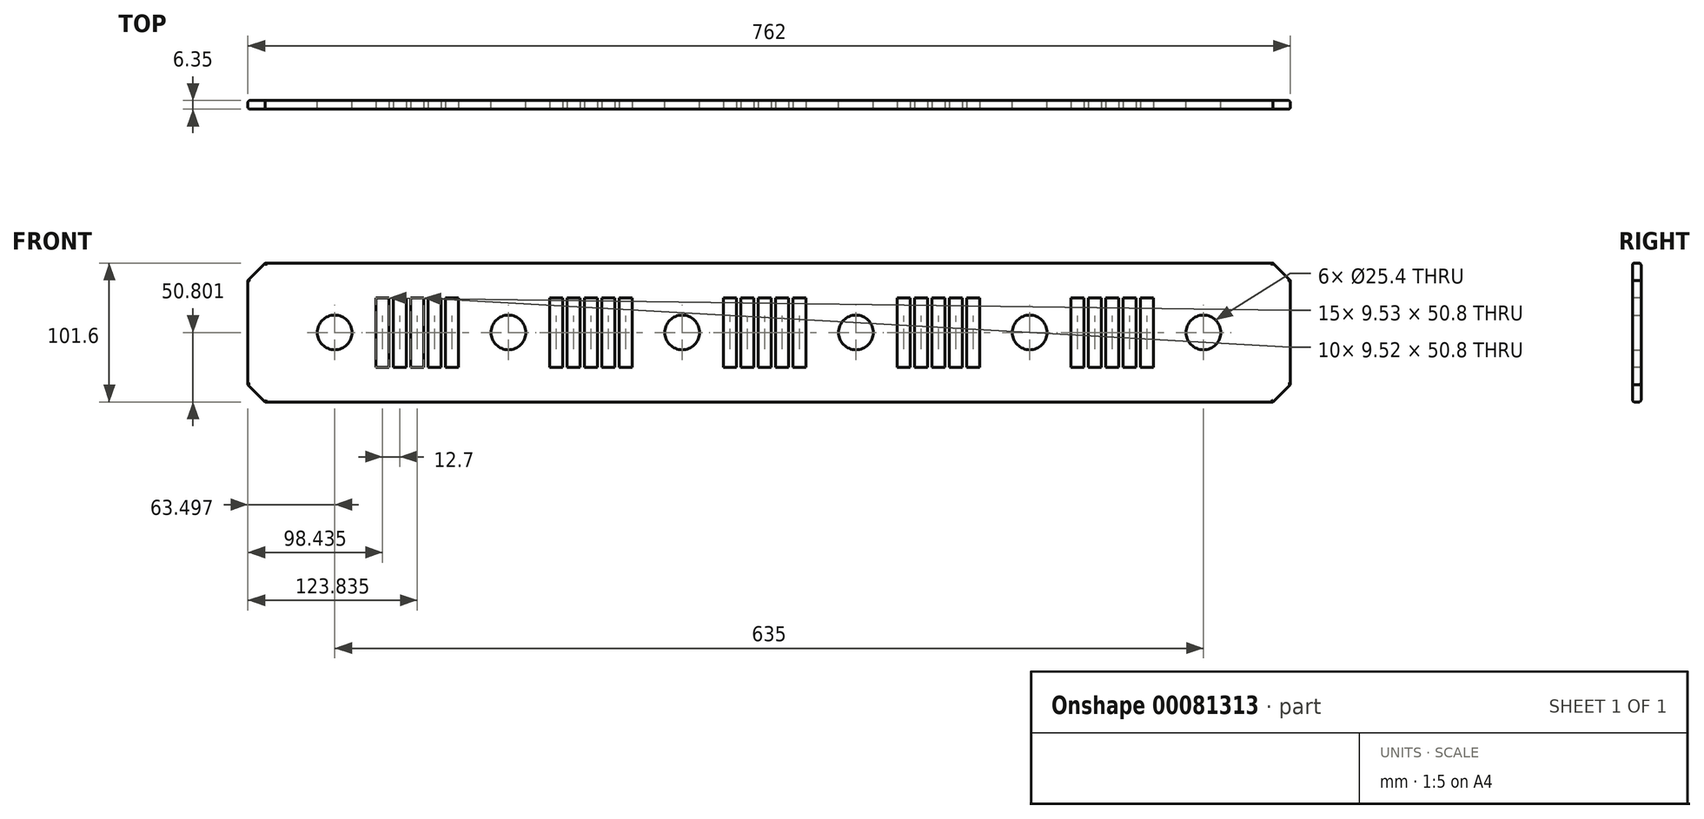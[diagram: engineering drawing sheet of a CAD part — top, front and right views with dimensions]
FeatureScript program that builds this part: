
annotation { "Feature Type Name" : "Feature", "Feature Type Description" : "" }
export const myFeature = defineFeature(function(context is Context, id is Id, definition is map)
    precondition{}
    {
        {
            var Q0;
            Q0=qCreatedBy(makeId("Front.planeOp"),FACE);
            var sketch = newSketch(context, id + "F0", { "sketchPlane" : qUnion([Q0])});
            skLineSegment(sketch, "E0", {"start": v(-386.11, -75.58) * mm, "end": v(375.89, -75.58) * mm});
            skLineSegment(sketch, "E1", {"start": v(375.89, -75.58) * mm, "end": v(375.89, -177.18) * mm});
            skLineSegment(sketch, "E2", {"start": v(375.89, -177.18) * mm, "end": v(-386.11, -177.18) * mm});
            skLineSegment(sketch, "E3", {"start": v(-386.11, -177.18) * mm, "end": v(-386.11, -75.58) * mm});
            skCircle(sketch, "E4", {"center": v(-322.61, -126.38) * mm, "radius": 12.7 * mm});
            skCircle(sketch, "E5", {"center": v(-195.61, -126.38) * mm, "radius": 12.7 * mm});
            skCircle(sketch, "E6", {"center": v(-68.61, -126.38) * mm, "radius": 12.7 * mm});
            skCircle(sketch, "E7", {"center": v(58.39, -126.38) * mm, "radius": 12.7 * mm});
            skCircle(sketch, "E8", {"center": v(185.39, -126.38) * mm, "radius": 12.7 * mm});
            skCircle(sketch, "E9", {"center": v(312.39, -126.38) * mm, "radius": 12.7 * mm});
            skSolve(sketch);
        }
        {
            var Q0;
            Q0 = qSketchRegion(id + "F0", true);
            extrude(context, id + "F1", {"entities" : qUnion([Q0]), "depth" : 6.35 * mm});
        }
        {
            var Q0;
            Q0=makeQuery(id+"F1.opExtrude","CAP_FACE",FACE,{"disambiguationData":[OSD([sQuery(id+"F0.wireOp",EDGE,"E0"),sQuery(id+"F0.wireOp",EDGE,"E1"),sQuery(id+"F0.wireOp",EDGE,"E2"),sQuery(id+"F0.wireOp",EDGE,"E3"),sQuery(id+"F0.wireOp",EDGE,"E4"),sQuery(id+"F0.wireOp",EDGE,"E5"),sQuery(id+"F0.wireOp",EDGE,"E7"),sQuery(id+"F0.wireOp",EDGE,"E6"),sQuery(id+"F0.wireOp",EDGE,"E8"),sQuery(id+"F0.wireOp",EDGE,"E9")])],"isStart":false});
            var sketch = newSketch(context, id + "F2", { "sketchPlane" : qUnion([Q0])});
            skLineSegment(sketch, "E10.bottom", {"start": v(-292.44, -100.98) * mm, "end": v(-282.91, -100.98) * mm});
            skLineSegment(sketch, "E10.top", {"start": v(-292.44, -151.78) * mm, "end": v(-282.91, -151.78) * mm});
            skLineSegment(sketch, "E10.left", {"start": v(-292.44, -100.98) * mm, "end": v(-292.44, -151.78) * mm});
            skLineSegment(sketch, "E10.right", {"start": v(-282.91, -100.98) * mm, "end": v(-282.91, -151.78) * mm});
            skLineSegment(sketch, "E11.1.0.0", {"start": v(-270.21, -100.98) * mm, "end": v(-270.21, -151.78) * mm});
            skLineSegment(sketch, "E11.1.0.1", {"start": v(-279.74, -100.98) * mm, "end": v(-279.74, -151.78) * mm});
            skLineSegment(sketch, "E11.1.0.2", {"start": v(-279.74, -151.78) * mm, "end": v(-270.21, -151.78) * mm});
            skLineSegment(sketch, "E11.1.0.3", {"start": v(-279.74, -100.98) * mm, "end": v(-270.21, -100.98) * mm});
            skLineSegment(sketch, "E11.2.0.0", {"start": v(-257.51, -100.98) * mm, "end": v(-257.51, -151.78) * mm});
            skLineSegment(sketch, "E11.2.0.1", {"start": v(-267.04, -100.98) * mm, "end": v(-267.04, -151.78) * mm});
            skLineSegment(sketch, "E11.2.0.2", {"start": v(-267.04, -151.78) * mm, "end": v(-257.51, -151.78) * mm});
            skLineSegment(sketch, "E11.2.0.3", {"start": v(-267.04, -100.98) * mm, "end": v(-257.51, -100.98) * mm});
            skLineSegment(sketch, "E11.3.0.0", {"start": v(-244.81, -100.98) * mm, "end": v(-244.81, -151.78) * mm});
            skLineSegment(sketch, "E11.3.0.1", {"start": v(-254.34, -100.98) * mm, "end": v(-254.34, -151.78) * mm});
            skLineSegment(sketch, "E11.3.0.2", {"start": v(-254.34, -151.78) * mm, "end": v(-244.81, -151.78) * mm});
            skLineSegment(sketch, "E11.3.0.3", {"start": v(-254.34, -100.98) * mm, "end": v(-244.81, -100.98) * mm});
            skLineSegment(sketch, "E11.4.0.0", {"start": v(-232.11, -100.98) * mm, "end": v(-232.11, -151.78) * mm});
            skLineSegment(sketch, "E11.4.0.1", {"start": v(-241.64, -100.98) * mm, "end": v(-241.64, -151.78) * mm});
            skLineSegment(sketch, "E11.4.0.2", {"start": v(-241.64, -151.78) * mm, "end": v(-232.11, -151.78) * mm});
            skLineSegment(sketch, "E11.4.0.3", {"start": v(-241.64, -100.98) * mm, "end": v(-232.11, -100.98) * mm});
            skLineSegment(sketch, "E11.direction1", {"start": v(-282.91, -151.78) * mm, "end": v(-270.21, -151.78) * mm, "construction": true});
            skLineSegment(sketch, "E12.bottom", {"start": v(-165.44, -100.98) * mm, "end": v(-155.91, -100.98) * mm});
            skLineSegment(sketch, "E12.top", {"start": v(-165.44, -151.78) * mm, "end": v(-155.91, -151.78) * mm});
            skLineSegment(sketch, "E12.left", {"start": v(-165.44, -100.98) * mm, "end": v(-165.44, -151.78) * mm});
            skLineSegment(sketch, "E12.right", {"start": v(-155.91, -100.98) * mm, "end": v(-155.91, -151.78) * mm});
            skLineSegment(sketch, "E13.1.0.0", {"start": v(-143.21, -100.98) * mm, "end": v(-143.21, -151.78) * mm});
            skLineSegment(sketch, "E13.1.0.1", {"start": v(-152.74, -100.98) * mm, "end": v(-152.74, -151.78) * mm});
            skLineSegment(sketch, "E13.1.0.2", {"start": v(-152.74, -151.78) * mm, "end": v(-143.21, -151.78) * mm});
            skLineSegment(sketch, "E13.1.0.3", {"start": v(-152.74, -100.98) * mm, "end": v(-143.21, -100.98) * mm});
            skLineSegment(sketch, "E13.2.0.0", {"start": v(-130.51, -100.98) * mm, "end": v(-130.51, -151.78) * mm});
            skLineSegment(sketch, "E13.2.0.1", {"start": v(-140.04, -100.98) * mm, "end": v(-140.04, -151.78) * mm});
            skLineSegment(sketch, "E13.2.0.2", {"start": v(-140.04, -151.78) * mm, "end": v(-130.51, -151.78) * mm});
            skLineSegment(sketch, "E13.2.0.3", {"start": v(-140.04, -100.98) * mm, "end": v(-130.51, -100.98) * mm});
            skLineSegment(sketch, "E13.3.0.0", {"start": v(-117.81, -100.98) * mm, "end": v(-117.81, -151.78) * mm});
            skLineSegment(sketch, "E13.3.0.1", {"start": v(-127.34, -100.98) * mm, "end": v(-127.34, -151.78) * mm});
            skLineSegment(sketch, "E13.3.0.2", {"start": v(-127.34, -151.78) * mm, "end": v(-117.81, -151.78) * mm});
            skLineSegment(sketch, "E13.3.0.3", {"start": v(-127.34, -100.98) * mm, "end": v(-117.81, -100.98) * mm});
            skLineSegment(sketch, "E13.4.0.0", {"start": v(-105.11, -100.98) * mm, "end": v(-105.11, -151.78) * mm});
            skLineSegment(sketch, "E13.4.0.1", {"start": v(-114.64, -100.98) * mm, "end": v(-114.64, -151.78) * mm});
            skLineSegment(sketch, "E13.4.0.2", {"start": v(-114.64, -151.78) * mm, "end": v(-105.11, -151.78) * mm});
            skLineSegment(sketch, "E13.4.0.3", {"start": v(-114.64, -100.98) * mm, "end": v(-105.11, -100.98) * mm});
            skLineSegment(sketch, "E13.direction1", {"start": v(-155.91, -151.78) * mm, "end": v(-143.21, -151.78) * mm, "construction": true});
            skLineSegment(sketch, "E14.bottom", {"start": v(-38.44, -100.98) * mm, "end": v(-28.91, -100.98) * mm});
            skLineSegment(sketch, "E14.top", {"start": v(-38.44, -151.78) * mm, "end": v(-28.91, -151.78) * mm});
            skLineSegment(sketch, "E14.left", {"start": v(-38.44, -100.98) * mm, "end": v(-38.44, -151.78) * mm});
            skLineSegment(sketch, "E14.right", {"start": v(-28.91, -100.98) * mm, "end": v(-28.91, -151.78) * mm});
            skLineSegment(sketch, "E15.1.0.0", {"start": v(-16.21, -100.98) * mm, "end": v(-16.21, -151.78) * mm});
            skLineSegment(sketch, "E15.1.0.1", {"start": v(-25.74, -100.98) * mm, "end": v(-25.74, -151.78) * mm});
            skLineSegment(sketch, "E15.1.0.2", {"start": v(-25.74, -151.78) * mm, "end": v(-16.21, -151.78) * mm});
            skLineSegment(sketch, "E15.1.0.3", {"start": v(-25.74, -100.98) * mm, "end": v(-16.21, -100.98) * mm});
            skLineSegment(sketch, "E15.2.0.0", {"start": v(-3.51, -100.98) * mm, "end": v(-3.51, -151.78) * mm});
            skLineSegment(sketch, "E15.2.0.1", {"start": v(-13.04, -100.98) * mm, "end": v(-13.04, -151.78) * mm});
            skLineSegment(sketch, "E15.2.0.2", {"start": v(-13.04, -151.78) * mm, "end": v(-3.51, -151.78) * mm});
            skLineSegment(sketch, "E15.2.0.3", {"start": v(-13.04, -100.98) * mm, "end": v(-3.51, -100.98) * mm});
            skLineSegment(sketch, "E15.3.0.0", {"start": v(9.19, -100.98) * mm, "end": v(9.19, -151.78) * mm});
            skLineSegment(sketch, "E15.3.0.1", {"start": v(-0.34, -100.98) * mm, "end": v(-0.34, -151.78) * mm});
            skLineSegment(sketch, "E15.3.0.2", {"start": v(-0.34, -151.78) * mm, "end": v(9.19, -151.78) * mm});
            skLineSegment(sketch, "E15.3.0.3", {"start": v(-0.34, -100.98) * mm, "end": v(9.19, -100.98) * mm});
            skLineSegment(sketch, "E15.4.0.0", {"start": v(21.89, -100.98) * mm, "end": v(21.89, -151.78) * mm});
            skLineSegment(sketch, "E15.4.0.1", {"start": v(12.36, -100.98) * mm, "end": v(12.36, -151.78) * mm});
            skLineSegment(sketch, "E15.4.0.2", {"start": v(12.36, -151.78) * mm, "end": v(21.89, -151.78) * mm});
            skLineSegment(sketch, "E15.4.0.3", {"start": v(12.36, -100.98) * mm, "end": v(21.89, -100.98) * mm});
            skLineSegment(sketch, "E15.direction1", {"start": v(-28.91, -151.78) * mm, "end": v(-16.21, -151.78) * mm, "construction": true});
            skLineSegment(sketch, "E16.bottom", {"start": v(88.56, -100.98) * mm, "end": v(98.09, -100.98) * mm});
            skLineSegment(sketch, "E16.top", {"start": v(88.56, -151.78) * mm, "end": v(98.09, -151.78) * mm});
            skLineSegment(sketch, "E16.left", {"start": v(88.56, -100.98) * mm, "end": v(88.56, -151.78) * mm});
            skLineSegment(sketch, "E16.right", {"start": v(98.09, -100.98) * mm, "end": v(98.09, -151.78) * mm});
            skLineSegment(sketch, "E17.1.0.0", {"start": v(110.79, -100.98) * mm, "end": v(110.79, -151.78) * mm});
            skLineSegment(sketch, "E17.1.0.1", {"start": v(101.26, -100.98) * mm, "end": v(101.26, -151.78) * mm});
            skLineSegment(sketch, "E17.1.0.2", {"start": v(101.26, -151.78) * mm, "end": v(110.79, -151.78) * mm});
            skLineSegment(sketch, "E17.1.0.3", {"start": v(101.26, -100.98) * mm, "end": v(110.79, -100.98) * mm});
            skLineSegment(sketch, "E17.2.0.0", {"start": v(123.49, -100.98) * mm, "end": v(123.49, -151.78) * mm});
            skLineSegment(sketch, "E17.2.0.1", {"start": v(113.96, -100.98) * mm, "end": v(113.96, -151.78) * mm});
            skLineSegment(sketch, "E17.2.0.2", {"start": v(113.96, -151.78) * mm, "end": v(123.49, -151.78) * mm});
            skLineSegment(sketch, "E17.2.0.3", {"start": v(113.96, -100.98) * mm, "end": v(123.49, -100.98) * mm});
            skLineSegment(sketch, "E17.3.0.0", {"start": v(136.19, -100.98) * mm, "end": v(136.19, -151.78) * mm});
            skLineSegment(sketch, "E17.3.0.1", {"start": v(126.66, -100.98) * mm, "end": v(126.66, -151.78) * mm});
            skLineSegment(sketch, "E17.3.0.2", {"start": v(126.66, -151.78) * mm, "end": v(136.19, -151.78) * mm});
            skLineSegment(sketch, "E17.3.0.3", {"start": v(126.66, -100.98) * mm, "end": v(136.19, -100.98) * mm});
            skLineSegment(sketch, "E17.4.0.0", {"start": v(148.89, -100.98) * mm, "end": v(148.89, -151.78) * mm});
            skLineSegment(sketch, "E17.4.0.1", {"start": v(139.36, -100.98) * mm, "end": v(139.36, -151.78) * mm});
            skLineSegment(sketch, "E17.4.0.2", {"start": v(139.36, -151.78) * mm, "end": v(148.89, -151.78) * mm});
            skLineSegment(sketch, "E17.4.0.3", {"start": v(139.36, -100.98) * mm, "end": v(148.89, -100.98) * mm});
            skLineSegment(sketch, "E17.direction1", {"start": v(98.09, -151.78) * mm, "end": v(110.79, -151.78) * mm, "construction": true});
            skLineSegment(sketch, "E18.bottom", {"start": v(215.56, -100.98) * mm, "end": v(225.09, -100.98) * mm});
            skLineSegment(sketch, "E18.top", {"start": v(215.56, -151.78) * mm, "end": v(225.09, -151.78) * mm});
            skLineSegment(sketch, "E18.left", {"start": v(215.56, -100.98) * mm, "end": v(215.56, -151.78) * mm});
            skLineSegment(sketch, "E18.right", {"start": v(225.09, -100.98) * mm, "end": v(225.09, -151.78) * mm});
            skLineSegment(sketch, "E19.1.0.0", {"start": v(237.79, -100.98) * mm, "end": v(237.79, -151.78) * mm});
            skLineSegment(sketch, "E19.1.0.1", {"start": v(228.26, -100.98) * mm, "end": v(228.26, -151.78) * mm});
            skLineSegment(sketch, "E19.1.0.2", {"start": v(228.26, -151.78) * mm, "end": v(237.79, -151.78) * mm});
            skLineSegment(sketch, "E19.1.0.3", {"start": v(228.26, -100.98) * mm, "end": v(237.79, -100.98) * mm});
            skLineSegment(sketch, "E19.2.0.0", {"start": v(250.49, -100.98) * mm, "end": v(250.49, -151.78) * mm});
            skLineSegment(sketch, "E19.2.0.1", {"start": v(240.96, -100.98) * mm, "end": v(240.96, -151.78) * mm});
            skLineSegment(sketch, "E19.2.0.2", {"start": v(240.96, -151.78) * mm, "end": v(250.49, -151.78) * mm});
            skLineSegment(sketch, "E19.2.0.3", {"start": v(240.96, -100.98) * mm, "end": v(250.49, -100.98) * mm});
            skLineSegment(sketch, "E19.3.0.0", {"start": v(263.19, -100.98) * mm, "end": v(263.19, -151.78) * mm});
            skLineSegment(sketch, "E19.3.0.1", {"start": v(253.66, -100.98) * mm, "end": v(253.66, -151.78) * mm});
            skLineSegment(sketch, "E19.3.0.2", {"start": v(253.66, -151.78) * mm, "end": v(263.19, -151.78) * mm});
            skLineSegment(sketch, "E19.3.0.3", {"start": v(253.66, -100.98) * mm, "end": v(263.19, -100.98) * mm});
            skLineSegment(sketch, "E19.4.0.0", {"start": v(275.89, -100.98) * mm, "end": v(275.89, -151.78) * mm});
            skLineSegment(sketch, "E19.4.0.1", {"start": v(266.36, -100.98) * mm, "end": v(266.36, -151.78) * mm});
            skLineSegment(sketch, "E19.4.0.2", {"start": v(266.36, -151.78) * mm, "end": v(275.89, -151.78) * mm});
            skLineSegment(sketch, "E19.4.0.3", {"start": v(266.36, -100.98) * mm, "end": v(275.89, -100.98) * mm});
            skLineSegment(sketch, "E19.direction1", {"start": v(225.09, -151.78) * mm, "end": v(237.79, -151.78) * mm, "construction": true});
            skSolve(sketch);
        }
        {
            var Q0;
            Q0 = qSketchRegion(id + "F2", true);
            extrude(context, id + "F3", {"entities" : qUnion([Q0]), "operationType" : NewBodyOperationType.REMOVE, "endBound" : BoundingType.THROUGH_ALL, "oppositeDirection" : true, "depth" : 25.4 * mm});
        }
        {
            var Q0;
            Q0=makeQuery(id+"F1.opExtrude","SWEPT_EDGE",EDGE,{"disambiguationData":[OSD([sQuery(id+"F0.wireOp",EDGE,"E0"),sQuery(id+"F0.wireOp",EDGE,"E3")])]});
            var Q1;
            Q1=makeQuery(id+"F1.opExtrude","SWEPT_EDGE",EDGE,{"disambiguationData":[OSD([sQuery(id+"F0.wireOp",EDGE,"E2"),sQuery(id+"F0.wireOp",EDGE,"E3")])]});
            var Q2;
            Q2=makeQuery(id+"F1.opExtrude","SWEPT_EDGE",EDGE,{"disambiguationData":[OSD([sQuery(id+"F0.wireOp",EDGE,"E0"),sQuery(id+"F0.wireOp",EDGE,"E1")])]});
            var Q3;
            Q3=makeQuery(id+"F1.opExtrude","SWEPT_EDGE",EDGE,{"disambiguationData":[OSD([sQuery(id+"F0.wireOp",EDGE,"E1"),sQuery(id+"F0.wireOp",EDGE,"E2")])]});
            chamfer(context, id + "F4", {"entities" : qUnion([Q0, Q1, Q2, Q3]), "width" : 12.7 * mm, "tangentPropagation" : true});
        }
        {
            var Q0;
            Q0=makeQuery(id+"F1.opExtrude","CAP_EDGE",EDGE,{"disambiguationData":[OSD([sQuery(id+"F0.wireOp",EDGE,"E2")])],"isStart":false});
            var Q1;
            Q1=makeQuery(id+"F1.opExtrude","CAP_EDGE",EDGE,{"disambiguationData":[OSD([sQuery(id+"F0.wireOp",EDGE,"E2")])],"isStart":true});
            var Q2;
            {var subQ0=sQuery(id+"F0.wireOp",EDGE,"E2");var subQ1=sQuery(id+"F0.wireOp",EDGE,"E1");Q2=makeQuery(id+"F4.opChamfer","BLEND_EDGE",EDGE,{"blendedFrom":[makeQuery(id+"F1.opExtrude","SWEPT_EDGE",EDGE,{"disambiguationData":[OSD([subQ1,subQ0])]}),makeQuery(id+"F1.opExtrude","CAP_FACE",FACE,{"disambiguationData":[OSD([sQuery(id+"F0.wireOp",EDGE,"E0"),subQ1,subQ0,sQuery(id+"F0.wireOp",EDGE,"E3"),sQuery(id+"F0.wireOp",EDGE,"E4"),sQuery(id+"F0.wireOp",EDGE,"E5"),sQuery(id+"F0.wireOp",EDGE,"E7"),sQuery(id+"F0.wireOp",EDGE,"E6"),sQuery(id+"F0.wireOp",EDGE,"E8"),sQuery(id+"F0.wireOp",EDGE,"E9")])],"isStart":false})],"blendedInto":[makeQuery(id+"F1.opExtrude","CAP_FACE",FACE,{"disambiguationData":[OSD([sQuery(id+"F0.wireOp",EDGE,"E0"),subQ1,subQ0,sQuery(id+"F0.wireOp",EDGE,"E3"),sQuery(id+"F0.wireOp",EDGE,"E4"),sQuery(id+"F0.wireOp",EDGE,"E5"),sQuery(id+"F0.wireOp",EDGE,"E7"),sQuery(id+"F0.wireOp",EDGE,"E6"),sQuery(id+"F0.wireOp",EDGE,"E8"),sQuery(id+"F0.wireOp",EDGE,"E9")])],"isStart":false})]});}
            var Q3;
            Q3=makeQuery(id+"F1.opExtrude","CAP_EDGE",EDGE,{"disambiguationData":[OSD([sQuery(id+"F0.wireOp",EDGE,"E1")])],"isStart":false});
            var Q4;
            {var subQ0=sQuery(id+"F0.wireOp",EDGE,"E2");var subQ1=sQuery(id+"F0.wireOp",EDGE,"E1");Q4=makeQuery(id+"F4.opChamfer","BLEND_EDGE",EDGE,{"blendedFrom":[makeQuery(id+"F1.opExtrude","SWEPT_EDGE",EDGE,{"disambiguationData":[OSD([subQ1,subQ0])]}),makeQuery(id+"F1.opExtrude","CAP_FACE",FACE,{"disambiguationData":[OSD([sQuery(id+"F0.wireOp",EDGE,"E0"),subQ1,subQ0,sQuery(id+"F0.wireOp",EDGE,"E3"),sQuery(id+"F0.wireOp",EDGE,"E4"),sQuery(id+"F0.wireOp",EDGE,"E5"),sQuery(id+"F0.wireOp",EDGE,"E7"),sQuery(id+"F0.wireOp",EDGE,"E6"),sQuery(id+"F0.wireOp",EDGE,"E8"),sQuery(id+"F0.wireOp",EDGE,"E9")])],"isStart":true})],"blendedInto":[makeQuery(id+"F1.opExtrude","CAP_FACE",FACE,{"disambiguationData":[OSD([sQuery(id+"F0.wireOp",EDGE,"E0"),subQ1,subQ0,sQuery(id+"F0.wireOp",EDGE,"E3"),sQuery(id+"F0.wireOp",EDGE,"E4"),sQuery(id+"F0.wireOp",EDGE,"E5"),sQuery(id+"F0.wireOp",EDGE,"E7"),sQuery(id+"F0.wireOp",EDGE,"E6"),sQuery(id+"F0.wireOp",EDGE,"E8"),sQuery(id+"F0.wireOp",EDGE,"E9")])],"isStart":true})]});}
            var Q5;
            Q5=makeQuery(id+"F1.opExtrude","CAP_EDGE",EDGE,{"disambiguationData":[OSD([sQuery(id+"F0.wireOp",EDGE,"E1")])],"isStart":true});
            var Q6;
            {var subQ0=sQuery(id+"F0.wireOp",EDGE,"E1");var subQ1=sQuery(id+"F0.wireOp",EDGE,"E0");Q6=makeQuery(id+"F4.opChamfer","BLEND_EDGE",EDGE,{"blendedFrom":[makeQuery(id+"F1.opExtrude","SWEPT_EDGE",EDGE,{"disambiguationData":[OSD([subQ1,subQ0])]}),makeQuery(id+"F1.opExtrude","CAP_FACE",FACE,{"disambiguationData":[OSD([subQ1,subQ0,sQuery(id+"F0.wireOp",EDGE,"E2"),sQuery(id+"F0.wireOp",EDGE,"E3"),sQuery(id+"F0.wireOp",EDGE,"E4"),sQuery(id+"F0.wireOp",EDGE,"E5"),sQuery(id+"F0.wireOp",EDGE,"E7"),sQuery(id+"F0.wireOp",EDGE,"E6"),sQuery(id+"F0.wireOp",EDGE,"E8"),sQuery(id+"F0.wireOp",EDGE,"E9")])],"isStart":false})],"blendedInto":[makeQuery(id+"F1.opExtrude","CAP_FACE",FACE,{"disambiguationData":[OSD([subQ1,subQ0,sQuery(id+"F0.wireOp",EDGE,"E2"),sQuery(id+"F0.wireOp",EDGE,"E3"),sQuery(id+"F0.wireOp",EDGE,"E4"),sQuery(id+"F0.wireOp",EDGE,"E5"),sQuery(id+"F0.wireOp",EDGE,"E7"),sQuery(id+"F0.wireOp",EDGE,"E6"),sQuery(id+"F0.wireOp",EDGE,"E8"),sQuery(id+"F0.wireOp",EDGE,"E9")])],"isStart":false})]});}
            var Q7;
            {var subQ0=sQuery(id+"F0.wireOp",EDGE,"E1");var subQ1=sQuery(id+"F0.wireOp",EDGE,"E0");Q7=makeQuery(id+"F4.opChamfer","BLEND_EDGE",EDGE,{"blendedFrom":[makeQuery(id+"F1.opExtrude","SWEPT_EDGE",EDGE,{"disambiguationData":[OSD([subQ1,subQ0])]}),makeQuery(id+"F1.opExtrude","CAP_FACE",FACE,{"disambiguationData":[OSD([subQ1,subQ0,sQuery(id+"F0.wireOp",EDGE,"E2"),sQuery(id+"F0.wireOp",EDGE,"E3"),sQuery(id+"F0.wireOp",EDGE,"E4"),sQuery(id+"F0.wireOp",EDGE,"E5"),sQuery(id+"F0.wireOp",EDGE,"E7"),sQuery(id+"F0.wireOp",EDGE,"E6"),sQuery(id+"F0.wireOp",EDGE,"E8"),sQuery(id+"F0.wireOp",EDGE,"E9")])],"isStart":true})],"blendedInto":[makeQuery(id+"F1.opExtrude","CAP_FACE",FACE,{"disambiguationData":[OSD([subQ1,subQ0,sQuery(id+"F0.wireOp",EDGE,"E2"),sQuery(id+"F0.wireOp",EDGE,"E3"),sQuery(id+"F0.wireOp",EDGE,"E4"),sQuery(id+"F0.wireOp",EDGE,"E5"),sQuery(id+"F0.wireOp",EDGE,"E7"),sQuery(id+"F0.wireOp",EDGE,"E6"),sQuery(id+"F0.wireOp",EDGE,"E8"),sQuery(id+"F0.wireOp",EDGE,"E9")])],"isStart":true})]});}
            var Q8;
            Q8=makeQuery(id+"F1.opExtrude","CAP_EDGE",EDGE,{"disambiguationData":[OSD([sQuery(id+"F0.wireOp",EDGE,"E0")])],"isStart":false});
            var Q9;
            Q9=makeQuery(id+"F1.opExtrude","CAP_EDGE",EDGE,{"disambiguationData":[OSD([sQuery(id+"F0.wireOp",EDGE,"E0")])],"isStart":true});
            var Q10;
            Q10=makeQuery(id+"F1.opExtrude","CAP_EDGE",EDGE,{"disambiguationData":[OSD([sQuery(id+"F0.wireOp",EDGE,"E3")])],"isStart":false});
            var Q11;
            Q11=makeQuery(id+"F1.opExtrude","CAP_EDGE",EDGE,{"disambiguationData":[OSD([sQuery(id+"F0.wireOp",EDGE,"E3")])],"isStart":true});
            var Q12;
            {var subQ0=sQuery(id+"F0.wireOp",EDGE,"E3");var subQ1=sQuery(id+"F0.wireOp",EDGE,"E2");Q12=makeQuery(id+"F4.opChamfer","BLEND_EDGE",EDGE,{"blendedFrom":[makeQuery(id+"F1.opExtrude","SWEPT_EDGE",EDGE,{"disambiguationData":[OSD([subQ1,subQ0])]}),makeQuery(id+"F1.opExtrude","CAP_FACE",FACE,{"disambiguationData":[OSD([sQuery(id+"F0.wireOp",EDGE,"E0"),sQuery(id+"F0.wireOp",EDGE,"E1"),subQ1,subQ0,sQuery(id+"F0.wireOp",EDGE,"E4"),sQuery(id+"F0.wireOp",EDGE,"E5"),sQuery(id+"F0.wireOp",EDGE,"E7"),sQuery(id+"F0.wireOp",EDGE,"E6"),sQuery(id+"F0.wireOp",EDGE,"E8"),sQuery(id+"F0.wireOp",EDGE,"E9")])],"isStart":false})],"blendedInto":[makeQuery(id+"F1.opExtrude","CAP_FACE",FACE,{"disambiguationData":[OSD([sQuery(id+"F0.wireOp",EDGE,"E0"),sQuery(id+"F0.wireOp",EDGE,"E1"),subQ1,subQ0,sQuery(id+"F0.wireOp",EDGE,"E4"),sQuery(id+"F0.wireOp",EDGE,"E5"),sQuery(id+"F0.wireOp",EDGE,"E7"),sQuery(id+"F0.wireOp",EDGE,"E6"),sQuery(id+"F0.wireOp",EDGE,"E8"),sQuery(id+"F0.wireOp",EDGE,"E9")])],"isStart":false})]});}
            var Q13;
            {var subQ0=sQuery(id+"F0.wireOp",EDGE,"E3");var subQ1=sQuery(id+"F0.wireOp",EDGE,"E2");Q13=makeQuery(id+"F4.opChamfer","BLEND_EDGE",EDGE,{"blendedFrom":[makeQuery(id+"F1.opExtrude","SWEPT_EDGE",EDGE,{"disambiguationData":[OSD([subQ1,subQ0])]}),makeQuery(id+"F1.opExtrude","CAP_FACE",FACE,{"disambiguationData":[OSD([sQuery(id+"F0.wireOp",EDGE,"E0"),sQuery(id+"F0.wireOp",EDGE,"E1"),subQ1,subQ0,sQuery(id+"F0.wireOp",EDGE,"E4"),sQuery(id+"F0.wireOp",EDGE,"E5"),sQuery(id+"F0.wireOp",EDGE,"E7"),sQuery(id+"F0.wireOp",EDGE,"E6"),sQuery(id+"F0.wireOp",EDGE,"E8"),sQuery(id+"F0.wireOp",EDGE,"E9")])],"isStart":true})],"blendedInto":[makeQuery(id+"F1.opExtrude","CAP_FACE",FACE,{"disambiguationData":[OSD([sQuery(id+"F0.wireOp",EDGE,"E0"),sQuery(id+"F0.wireOp",EDGE,"E1"),subQ1,subQ0,sQuery(id+"F0.wireOp",EDGE,"E4"),sQuery(id+"F0.wireOp",EDGE,"E5"),sQuery(id+"F0.wireOp",EDGE,"E7"),sQuery(id+"F0.wireOp",EDGE,"E6"),sQuery(id+"F0.wireOp",EDGE,"E8"),sQuery(id+"F0.wireOp",EDGE,"E9")])],"isStart":true})]});}
            var Q14;
            {var subQ0=sQuery(id+"F0.wireOp",EDGE,"E3");var subQ1=sQuery(id+"F0.wireOp",EDGE,"E0");Q14=makeQuery(id+"F4.opChamfer","BLEND_EDGE",EDGE,{"blendedFrom":[makeQuery(id+"F1.opExtrude","SWEPT_EDGE",EDGE,{"disambiguationData":[OSD([subQ1,subQ0])]}),makeQuery(id+"F1.opExtrude","CAP_FACE",FACE,{"disambiguationData":[OSD([subQ1,sQuery(id+"F0.wireOp",EDGE,"E1"),sQuery(id+"F0.wireOp",EDGE,"E2"),subQ0,sQuery(id+"F0.wireOp",EDGE,"E4"),sQuery(id+"F0.wireOp",EDGE,"E5"),sQuery(id+"F0.wireOp",EDGE,"E7"),sQuery(id+"F0.wireOp",EDGE,"E6"),sQuery(id+"F0.wireOp",EDGE,"E8"),sQuery(id+"F0.wireOp",EDGE,"E9")])],"isStart":false})],"blendedInto":[makeQuery(id+"F1.opExtrude","CAP_FACE",FACE,{"disambiguationData":[OSD([subQ1,sQuery(id+"F0.wireOp",EDGE,"E1"),sQuery(id+"F0.wireOp",EDGE,"E2"),subQ0,sQuery(id+"F0.wireOp",EDGE,"E4"),sQuery(id+"F0.wireOp",EDGE,"E5"),sQuery(id+"F0.wireOp",EDGE,"E7"),sQuery(id+"F0.wireOp",EDGE,"E6"),sQuery(id+"F0.wireOp",EDGE,"E8"),sQuery(id+"F0.wireOp",EDGE,"E9")])],"isStart":false})]});}
            var Q15;
            {var subQ0=sQuery(id+"F0.wireOp",EDGE,"E3");var subQ1=sQuery(id+"F0.wireOp",EDGE,"E0");Q15=makeQuery(id+"F4.opChamfer","BLEND_EDGE",EDGE,{"blendedFrom":[makeQuery(id+"F1.opExtrude","SWEPT_EDGE",EDGE,{"disambiguationData":[OSD([subQ1,subQ0])]}),makeQuery(id+"F1.opExtrude","CAP_FACE",FACE,{"disambiguationData":[OSD([subQ1,sQuery(id+"F0.wireOp",EDGE,"E1"),sQuery(id+"F0.wireOp",EDGE,"E2"),subQ0,sQuery(id+"F0.wireOp",EDGE,"E4"),sQuery(id+"F0.wireOp",EDGE,"E5"),sQuery(id+"F0.wireOp",EDGE,"E7"),sQuery(id+"F0.wireOp",EDGE,"E6"),sQuery(id+"F0.wireOp",EDGE,"E8"),sQuery(id+"F0.wireOp",EDGE,"E9")])],"isStart":true})],"blendedInto":[makeQuery(id+"F1.opExtrude","CAP_FACE",FACE,{"disambiguationData":[OSD([subQ1,sQuery(id+"F0.wireOp",EDGE,"E1"),sQuery(id+"F0.wireOp",EDGE,"E2"),subQ0,sQuery(id+"F0.wireOp",EDGE,"E4"),sQuery(id+"F0.wireOp",EDGE,"E5"),sQuery(id+"F0.wireOp",EDGE,"E7"),sQuery(id+"F0.wireOp",EDGE,"E6"),sQuery(id+"F0.wireOp",EDGE,"E8"),sQuery(id+"F0.wireOp",EDGE,"E9")])],"isStart":true})]});}
            fillet(context, id + "F5", {"entities" : qUnion([Q0, Q1, Q2, Q3, Q4, Q5, Q6, Q7, Q8, Q9, Q10, Q11, Q12, Q13, Q14, Q15]), "radius" : 1.6 * mm, "tangentPropagation" : true, "allowEdgeOverflow" : false});
        }
    });
